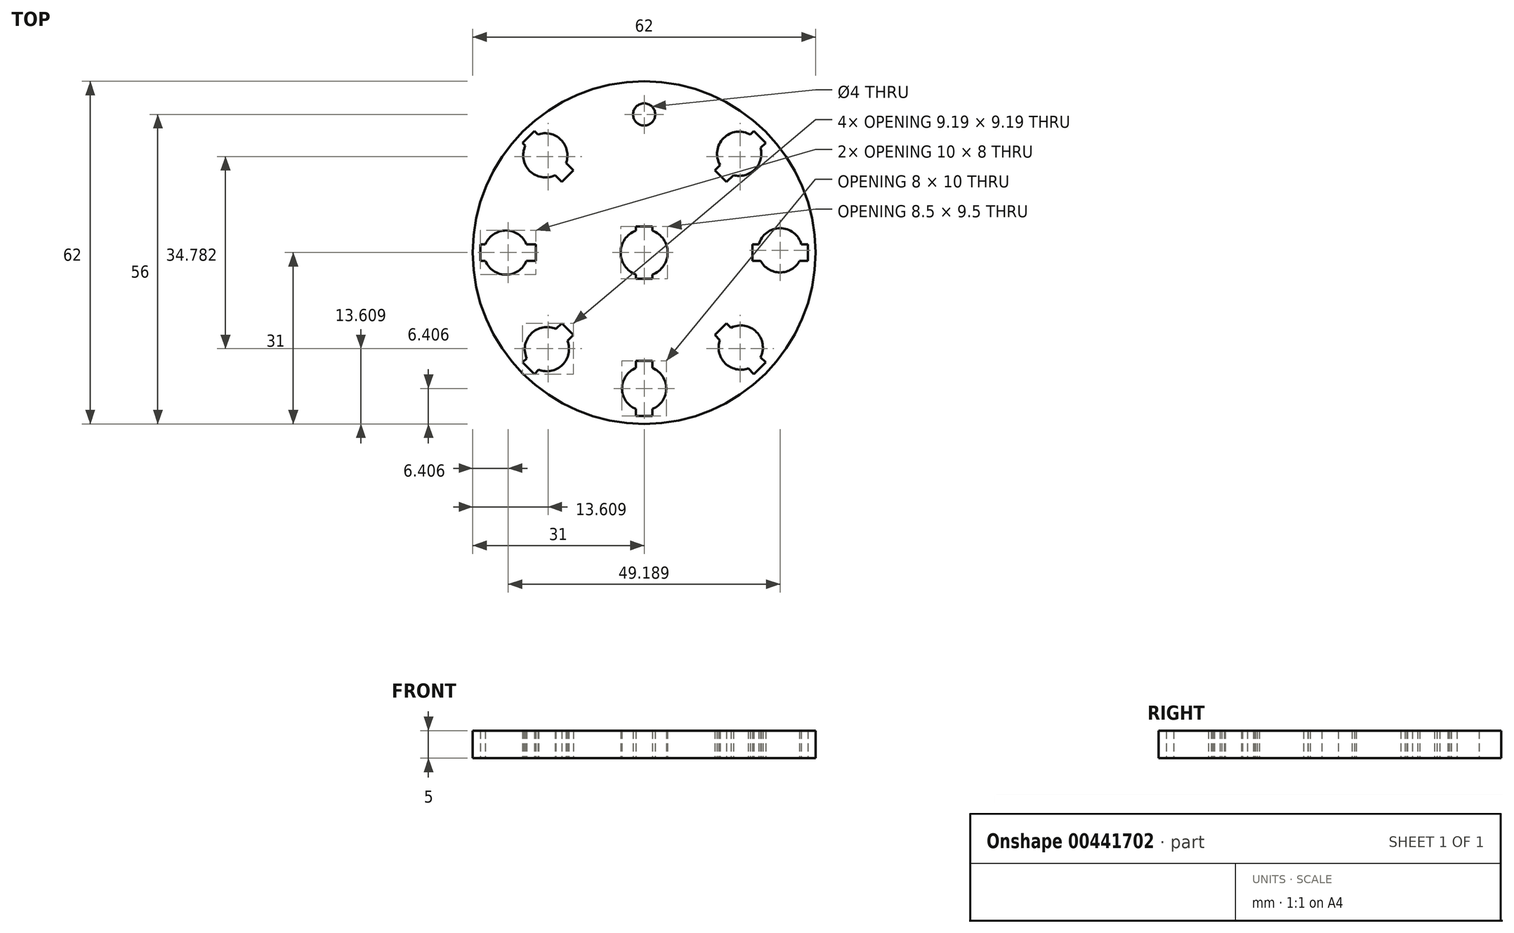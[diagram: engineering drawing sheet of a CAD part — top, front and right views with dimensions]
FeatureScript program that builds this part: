
annotation { "Feature Type Name" : "Feature", "Feature Type Description" : "" }
export const myFeature = defineFeature(function(context is Context, id is Id, definition is map)
    precondition{}
    {
        {
            var Q0;
            Q0=qCreatedBy(makeId("Top.planeOp"),FACE);
            var sketch = newSketch(context, id + "F0", { "sketchPlane" : qUnion([Q0])});
            skCircle(sketch, "E0", {"center": v(0, 0) * mm, "radius": 31 * mm});
            skCircle(sketch, "E1", {"center": v(0, 0) * mm, "radius": 4.25 * mm});
            skLineSegment(sketch, "E2", {"start": v(0, 51.46) * mm, "end": v(0, -49.24) * mm, "construction": true});
            skLineSegment(sketch, "E3", {"start": v(-46.2, 0) * mm, "end": v(46.41, 0) * mm, "construction": true});
            skCircle(sketch, "E4", {"center": v(-25, 0) * mm, "radius": 4 * mm});
            skCircle(sketch, "E5", {"center": v(0, 0) * mm, "radius": 25 * mm});
            skCircle(sketch, "E6.1.0", {"center": v(-17.6, -17.47) * mm, "radius": 4 * mm});
            skCircle(sketch, "E6.2.0", {"center": v(0, -24.6) * mm, "radius": 4 * mm});
            skCircle(sketch, "E6.3.0", {"center": v(17.47, -17.19) * mm, "radius": 4 * mm});
            skCircle(sketch, "E6.4.0", {"center": v(24.6, 0.4) * mm, "radius": 4 * mm});
            skCircle(sketch, "E6.5.0", {"center": v(17.19, 17.88) * mm, "radius": 4 * mm});
            skCircle(sketch, "E6.7.0", {"center": v(-17.88, 17.6) * mm, "radius": 4 * mm});
            skPoint(sketch, "E6.center", {"position": v(-0.2, 0.2) * mm});
            skLineSegment(sketch, "E7.bottom", {"start": v(-1.5, -19.6) * mm, "end": v(1.5, -19.6) * mm});
            skLineSegment(sketch, "E7.top", {"start": v(-1.5, -29.6) * mm, "end": v(1.5, -29.6) * mm});
            skLineSegment(sketch, "E7.left", {"start": v(-1.5, -19.6) * mm, "end": v(-1.5, -29.6) * mm});
            skLineSegment(sketch, "E7.right", {"start": v(1.5, -19.6) * mm, "end": v(1.5, -29.6) * mm});
            skLineSegment(sketch, "E8", {"start": v(-6.61, -24.6) * mm, "end": v(9.2, -24.6) * mm, "construction": true});
            skLineSegment(sketch, "E9.1.0", {"start": v(12.8, -14.92) * mm, "end": v(19.87, -21.99) * mm});
            skLineSegment(sketch, "E9.1.1", {"start": v(14.92, -12.8) * mm, "end": v(21.99, -19.87) * mm});
            skLineSegment(sketch, "E9.1.2", {"start": v(19.87, -21.99) * mm, "end": v(21.99, -19.87) * mm});
            skLineSegment(sketch, "E9.1.3", {"start": v(12.8, -14.92) * mm, "end": v(14.92, -12.8) * mm});
            skLineSegment(sketch, "E9.2.0", {"start": v(19.6, -1.5) * mm, "end": v(29.6, -1.5) * mm});
            skLineSegment(sketch, "E9.2.1", {"start": v(19.6, 1.5) * mm, "end": v(29.6, 1.5) * mm});
            skLineSegment(sketch, "E9.2.2", {"start": v(29.6, -1.5) * mm, "end": v(29.6, 1.5) * mm});
            skLineSegment(sketch, "E9.2.3", {"start": v(19.6, -1.5) * mm, "end": v(19.6, 1.5) * mm});
            skLineSegment(sketch, "E9.3.0", {"start": v(14.92, 12.8) * mm, "end": v(21.99, 19.87) * mm});
            skLineSegment(sketch, "E9.3.1", {"start": v(12.8, 14.92) * mm, "end": v(19.87, 21.99) * mm});
            skLineSegment(sketch, "E9.3.2", {"start": v(21.99, 19.87) * mm, "end": v(19.87, 21.99) * mm});
            skLineSegment(sketch, "E9.3.3", {"start": v(14.92, 12.8) * mm, "end": v(12.8, 14.92) * mm});
            skLineSegment(sketch, "E9.5.0", {"start": v(-12.8, 14.92) * mm, "end": v(-19.87, 21.99) * mm});
            skLineSegment(sketch, "E9.5.1", {"start": v(-14.92, 12.8) * mm, "end": v(-21.99, 19.87) * mm});
            skLineSegment(sketch, "E9.5.2", {"start": v(-19.87, 21.99) * mm, "end": v(-21.99, 19.87) * mm});
            skLineSegment(sketch, "E9.5.3", {"start": v(-12.8, 14.92) * mm, "end": v(-14.92, 12.8) * mm});
            skLineSegment(sketch, "E9.6.0", {"start": v(-19.6, 1.5) * mm, "end": v(-29.6, 1.5) * mm});
            skLineSegment(sketch, "E9.6.1", {"start": v(-19.6, -1.5) * mm, "end": v(-29.6, -1.5) * mm});
            skLineSegment(sketch, "E9.6.2", {"start": v(-29.6, 1.5) * mm, "end": v(-29.6, -1.5) * mm});
            skLineSegment(sketch, "E9.6.3", {"start": v(-19.6, 1.5) * mm, "end": v(-19.6, -1.5) * mm});
            skLineSegment(sketch, "E9.7.0", {"start": v(-14.92, -12.8) * mm, "end": v(-21.99, -19.87) * mm});
            skLineSegment(sketch, "E9.7.1", {"start": v(-12.8, -14.92) * mm, "end": v(-19.87, -21.99) * mm});
            skLineSegment(sketch, "E9.7.2", {"start": v(-21.99, -19.87) * mm, "end": v(-19.87, -21.99) * mm});
            skLineSegment(sketch, "E9.7.3", {"start": v(-14.92, -12.8) * mm, "end": v(-12.8, -14.92) * mm});
            skLineSegment(sketch, "E10.bottom", {"start": v(-1.5, 4.75) * mm, "end": v(1.5, 4.75) * mm});
            skLineSegment(sketch, "E10.top", {"start": v(-1.5, -4.75) * mm, "end": v(1.5, -4.75) * mm});
            skLineSegment(sketch, "E10.left", {"start": v(-1.5, 4.75) * mm, "end": v(-1.5, -4.75) * mm});
            skLineSegment(sketch, "E10.right", {"start": v(1.5, 4.75) * mm, "end": v(1.5, -4.75) * mm});
            skCircle(sketch, "E11", {"center": v(0, 25) * mm, "radius": 2 * mm});
            skSolve(sketch);
        }
        {
            var Q0;
            Q0=makeQuery(id+"F0.imprint","IMPRINT",FACE,{"disambiguationData":[TD([[makeQuery(id+"F0.imprint","IMPRINT",EDGE,{"derivedFrom":sQuery(id+"F0.wireOp",EDGE,"E1")}),-1.0]])]});
            var Q1;
            Q1=makeQuery(id+"F0.imprint","IMPRINT",FACE,{"disambiguationData":[TD([[makeQuery(id+"F0.imprint","IMPRINT",EDGE,{"derivedFrom":sQuery(id+"F0.wireOp",EDGE,"E0")}),1.0]])]});
            extrude(context, id + "F1", {"entities" : qUnion([Q0, Q1]), "depth" : 5 * mm});
        }
    });
